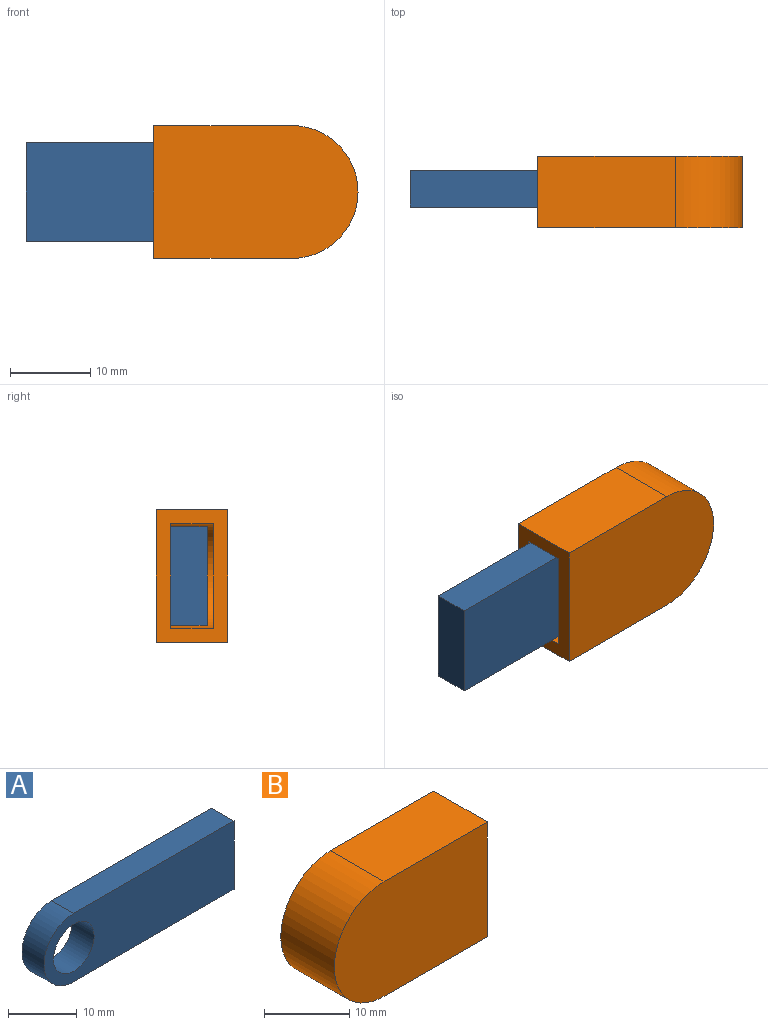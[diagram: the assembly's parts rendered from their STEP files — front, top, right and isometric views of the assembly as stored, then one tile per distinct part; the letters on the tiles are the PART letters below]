
ASSEMBLY  parts=2 mates=1
PART A: 7 faces, bbox 39.1x4.5x12.2 mm
  f0: plane 33.02x4.55mm, normal (0,0,-1), area 150.1mm2, adj f1,f3,f5,f6
  f1: plane 12.19x4.55mm, normal (1,0,0), area 55.4mm2, adj f0,f2,f5,f6
  f2: plane 33.02x4.55mm, normal (0,0,1), area 150.1mm2, adj f1,f3,f5,f6
  f3: cylinder r=6.1mm len=12.19mm, axis (0,1,0), area 87.1mm2, adj f0,f2,f5,f6
  f4: cylinder r=4.19mm len=8.38mm, axis (0,1,0), area 119.7mm2, adj f5,f6
  f5: plane 39.12x12.19mm, normal (0,-1,0), area 405.8mm2, adj f0,f1,f2,f3,f4
  f6: plane 39.12x12.19mm, normal (0,1,0), area 405.8mm2, adj f0,f1,f2,f3,f4
PART B: 11 faces, bbox 25.4x8.9x16.5 mm
  f0: plane 16.51x8.89mm, normal (1,0,0), area 77.7mm2, adj f1,f2,f4,f5,f6,f7,f9,f10
  f1: plane 17.15x8.89mm, normal (0,0,-1), area 152.4mm2, adj f0,f3,f4,f5
  f2: plane 17.15x8.89mm, normal (0,0,1), area 152.4mm2, adj f0,f3,f4,f5
  f3: cylinder r=8.26mm len=16.51mm, axis (0,1,0), area 230.6mm2, adj f1,f2,f4,f5
  f4: plane 25.4x16.51mm, normal (0,-1,0), area 390.1mm2, adj f0,f1,f2,f3
  f5: plane 25.4x16.51mm, normal (0,1,0), area 390.1mm2, adj f0,f1,f2,f3
  f6: plane 17.15x5.33mm, normal (0,0,1), area 91.5mm2, adj f0,f8,f9,f10
  f7: plane 17.15x5.33mm, normal (0,0,-1), area 91.5mm2, adj f0,f8,f9,f10
  f8: cylinder r=6.48mm len=12.95mm, axis (0,1,0), area 108.5mm2, adj f6,f7,f9,f10
  f9: plane 23.62x12.95mm, normal (0,1,0), area 288mm2, adj f0,f6,f7,f8
  f10: plane 23.62x12.95mm, normal (0,-1,0), area 288mm2, adj f0,f6,f7,f8
PLACE A rot(axis=(0,1,0),180deg) t=(118.75,-9.1,90.07)mm
PLACE B rot(axis=(0,0,-1),180deg) t=(113.17,-16.21,90.07)mm
MATE fastened A.f4 <-> B.f3  axis (0,1,0) through (134.71,-9.1,90.07)mm
